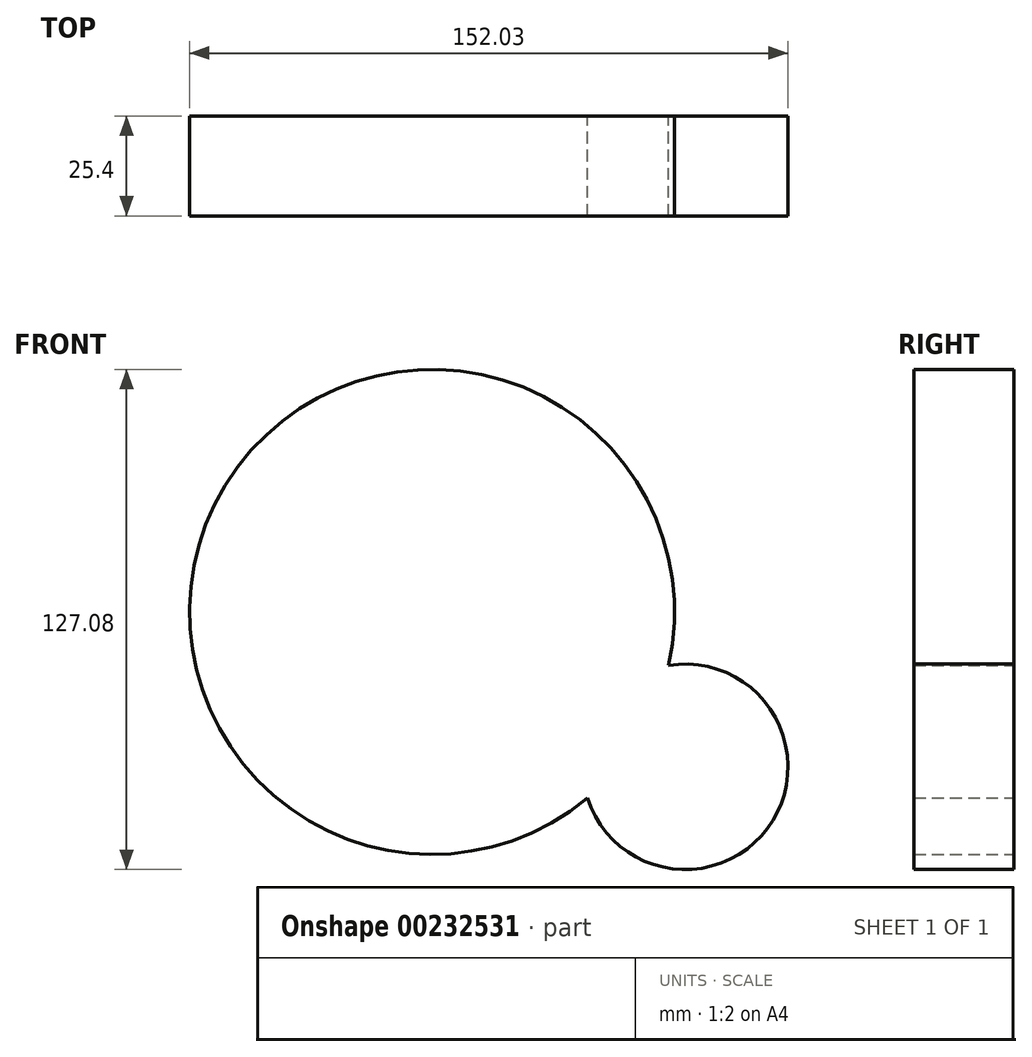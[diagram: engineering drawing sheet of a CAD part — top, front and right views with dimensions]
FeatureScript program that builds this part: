
annotation { "Feature Type Name" : "Feature", "Feature Type Description" : "" }
export const myFeature = defineFeature(function(context is Context, id is Id, definition is map)
    precondition{}
    {
        {
            var Q0;
            Q0=qCreatedBy(makeId("Front.planeOp"),FACE);
            var sketch = newSketch(context, id + "F0", { "sketchPlane" : qUnion([Q0])});
            skCircle(sketch, "E0", {"center": v(-64.32, 39.37) * mm, "radius": 61.6 * mm});
            skCircle(sketch, "E1", {"center": v(0, 0) * mm, "radius": 26.1 * mm});
            skSolve(sketch);
        }
        {
            var Q0;
            Q0 = qSketchRegion(id + "F0", true);
            extrude(context, id + "F1", {"entities" : qUnion([Q0]), "depth" : 25.4 * mm});
        }
    });
